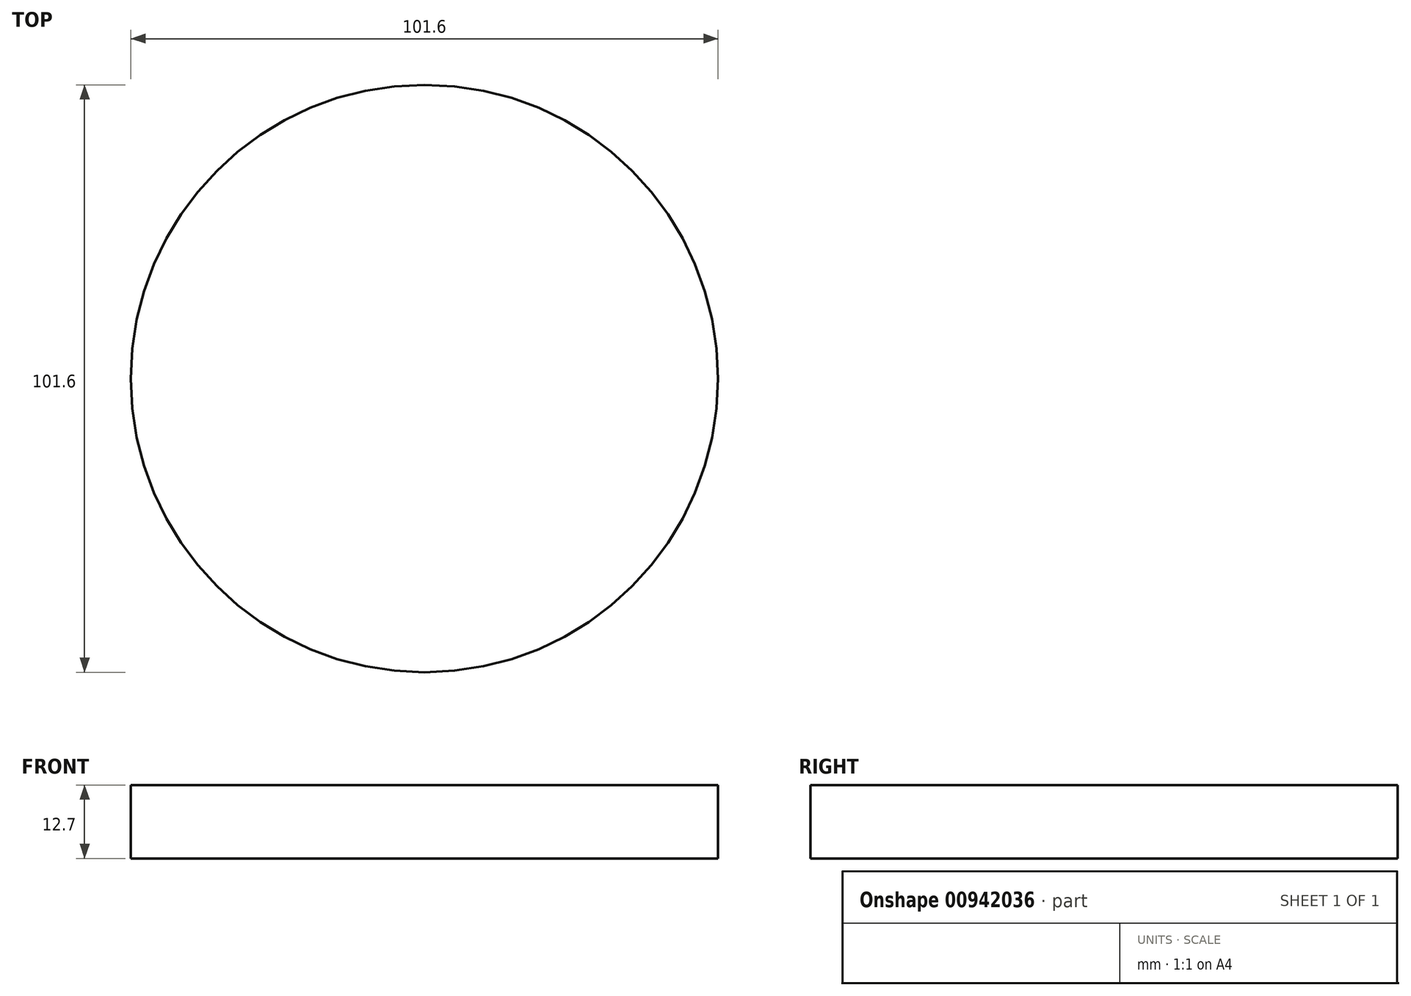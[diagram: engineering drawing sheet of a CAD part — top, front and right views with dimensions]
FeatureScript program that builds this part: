
annotation { "Feature Type Name" : "Feature", "Feature Type Description" : "" }
export const myFeature = defineFeature(function(context is Context, id is Id, definition is map)
    precondition{}
    {
        {
            var Q0;
            Q0=qCreatedBy(makeId("Top.planeOp"),FACE);
            var sketch = newSketch(context, id + "F0", { "sketchPlane" : qUnion([Q0])});
            skCircle(sketch, "E0", {"center": v(0, 0) * mm, "radius": 50.8 * mm});
            skSolve(sketch);
        }
        {
            var Q0;
            Q0=sQuery(id+"F0.wireOp",EDGE,"E0");
            extrude(context, id + "F1", {"bodyType" : ToolBodyType.SURFACE, "surfaceEntities" : qUnion([Q0]), "depth" : 12.7 * mm, "offsetDistance" : 25.4 * mm});
        }
    });
